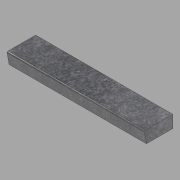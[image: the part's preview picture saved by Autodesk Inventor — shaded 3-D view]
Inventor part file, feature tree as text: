
AUTODESK INVENTOR PART (.ipt)
format: ipt  version: 2022.1 (Build 261234020, 234B)  size: 97,280 bytes
history: native  units: in
note: dims shown in document units (in); Inventor stores cm internally (conversion verified against a paired STEP export)
features: other x3, extrude x1, sketch x1
ambient origin geometry x8: Origin, YZ Plane, XZ Plane, XY Plane, X Axis, Y Axis, Z Axis, Center Point
bodies: Solid1 (feature_tree)
feature tree (5):
  other  "Blocks"
  extrude  "Extrusion1"  Depth=67.25in TaperAngle=0.0deg
  sketch  "Sketch1"  dims[d0=13.0in d1=6.0in d2=13.5in d3=0.5in d4=0.5in d5=67.25in d6=0.0in]
  other  "Profile"
  other  "Profile:1"
